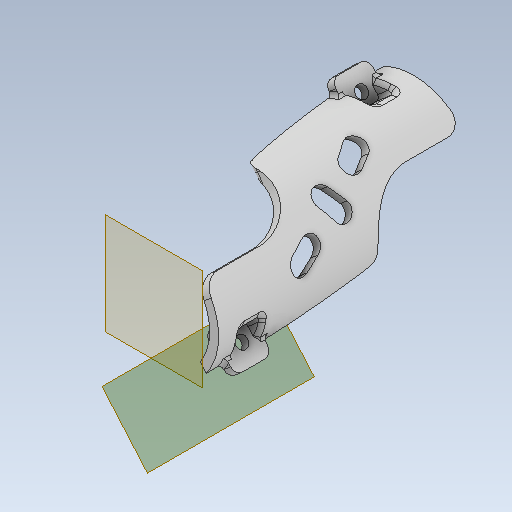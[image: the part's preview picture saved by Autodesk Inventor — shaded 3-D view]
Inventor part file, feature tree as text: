
AUTODESK INVENTOR PART (.ipt)
format: ipt  version: 2020 (Build 240168000, 168)  size: 538,112 bytes
history: native  units: mm
features: sketch x12, plane x4, other x3
ambient origin geometry x8: Origin, YZ Plane, XZ Plane, XY Plane, X Axis, Y Axis, Z Axis, Center Point
bodies: Solid1 (feature_tree)
feature tree (19):
  other  "protect_shell_1.ipt"
  other  "Solid2::protect_shell_1.ipt"
  other  "TaggingFeature1"
  sketch  "Sketch2"  dims[d0=10.0mm]
  sketch  "Sketch3"
  sketch  "Sketch4"
  sketch  "Sketch5"
  sketch  "Sketch6"
  sketch  "Sketch7"
  sketch  "Sketch8"
  sketch  "Sketch9"
  sketch  "Sketch10"
  sketch  "Sketch11"
  sketch  "Sketch12"
  sketch  "Sketch13"
  plane  "Work Plane1"
  plane  "Work Plane2"
  plane  "Work Plane3"
  plane  "Work Plane4"
